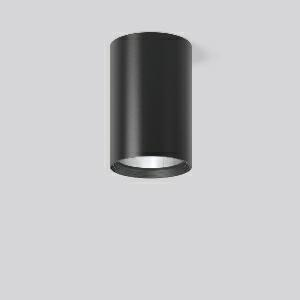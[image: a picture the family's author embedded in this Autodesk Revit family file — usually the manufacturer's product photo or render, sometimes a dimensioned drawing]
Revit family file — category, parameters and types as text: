
# Revit family: heledon_maxi_a_931230_003_4984
name_source: partatom
category: Lighting Fixtures
units: mm (PartAtom-declared; Revit-internal decimal feet)

## family parameters
Cut with Voids When Loaded = No
Host = Face
Light Source = No
Part Type = Normal
Room Calculation Point = No
Round Connector Dimension = Use Diameter
Shared = No

## types (1)
- HELEDON maxi A (1 x LED Modul 932 fresh meat, 2100 lm, 3200)
    Apparent Load = 33 VA
    Approval mark = CE
    CIE Flux Codes = 100 100 100 100 100
    Color Rendering = 90
    Color Temperature = 3200
    Default Elevation = 1800 mm
    Description = Series: HELEDON maxi
Cylindrical surface-mounted downlight. Housing: die-cast aluminium, powder-coated. Internal ceiling frame polycarbonate with bayonet mounting. Black plastic ring and recessed LED to prevent glare from the side. Optical assembly with reflector made of MIRO-Silver with 98% total light reflection for outstanding efficiency - can be changed without tools. Special LED for illumination of meat included. Suitable for Ceiling mounting. Easy installation with a separate ceiling frame with bayonet mounting and plug connection. Driver integrated. Connected via plug-in connector. High quality converter without flickering and stroboscopic effect. The following accessories can be mounted without use of tools: interchangeable lenses, decorative glasses, honeycomb louvre, clear and frosted diffusers, white interchangeable plastic ring. 
Colour: deep black, matt (RAL 9005)
Diameter: 123 mm
Height: 183 mm
Lamp: LED
Socket: without socket
Colour temperature: fresh meat
System power: 33 W
Rated luminous flux: 2100 lm
Luminous efficiency: 64 lm/W
Control gear: Regulated power supply
Protection class: I
Type of protection: IP 20
    Height = 183 mm
    Lamp = 1 x LED Modul 932 fresh meat
    Lamp Light Flux = 2100 lm
    Lamp count = 1
    Length = 123 mm
    Lifetime = 50000 h
    Luminous efficacy = 64 lm/W
    Manufacturer = RZB
    ModVariant = No
    Model = 931230.003
    Mounting Place = Ceiling
    Mounting Type = Surface mounted
    Number of Poles = 1
    OnlyDefault = Yes
    Power Factor = 1
    Product Name = HELEDON maxi A
    Product group = Surface mounted downlights
    ProductGroupID = 302
    Protection Class = Protection class I
    Protection Degree = IP 20
    RLX_Detail_Level = 1
    RLX_Emergency_Light_Flux = 0 lm
    RLX_Emergency_Type = 0
    RLX_Emergency_Type_DB = No
    RlxData = <blob elided: 97837 chars, md5=09fcaa1c>
    Socket = socket
    Standby Power = 0 W
    System Light Flux = 2100 lm
    System Power = 33 W
    Type Comments = Product without accessories
    Type Image = 931192.003.jpg
    URL = http://relux.com
    VarID = ---
    Voltage = 230 V
    Voltage Range = 220-240 V
    Weight = 0.00 kg
    Width = 0 mm  [stored 0 ft]

note: [stored X ft] marks values corroborated as IEEE doubles in the binary element streams (Revit-internal decimal feet)

## geometry (parser evidence)
native form markers: Blend x4, Sweep x10
no freeform markers — native parametric forms only
